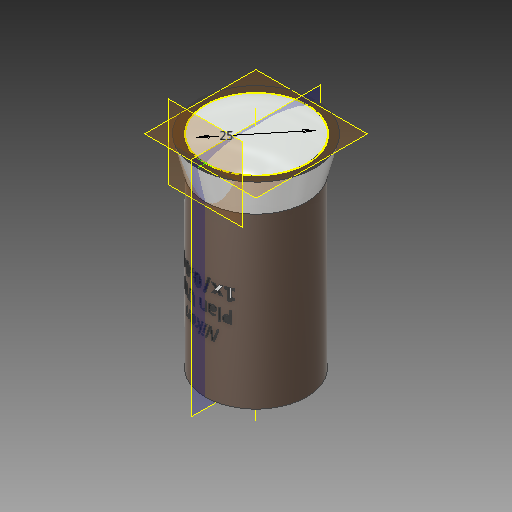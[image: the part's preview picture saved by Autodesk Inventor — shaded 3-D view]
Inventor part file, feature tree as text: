
AUTODESK INVENTOR PART (.ipt)
format: ipt  version: 2017 (Build 210142000, 142)  size: 686,592 bytes
history: native  units: mm
features: sketch x5, plane x3, other x2, extrude x1, loft x1, emboss x1, revolve x1
ambient origin geometry x8: Origin, YZ Plane, XZ Plane, XY Plane, X Axis, Y Axis, Z Axis, Center Point
bodies: Solid1 (feature_tree)
feature tree (14):
  extrude  "Extrusion1"  Depth=50.0mm TaperAngle=0.0deg
  plane  "Work Plane1"
  sketch  "Sketch2"  dims[d3=10.0mm d4=35.0mm]
  loft  "Loft1"
  other  "Work Axis1"
  plane  "Work Plane2"
  emboss  "Emboss1"
  plane  "Work Plane3"
  revolve  "Revolution1"  Angle=90.0deg
  sketch  "Sketch1"  dims[d0=30.0mm d1=50.0mm d2=0.0mm]
  sketch  "Sketch3"  dims[d5=0.0mm d6=90.0deg d7=0.0mm d8=90.0deg]
  other  "Edges1"
  sketch  "Sketch4"  dims[d9=1.0mm d10=0.0mm]
  sketch  "Sketch5"  dims[d11=25.0mm d12=90.0deg d13=15.0mm d14=90.0deg]
